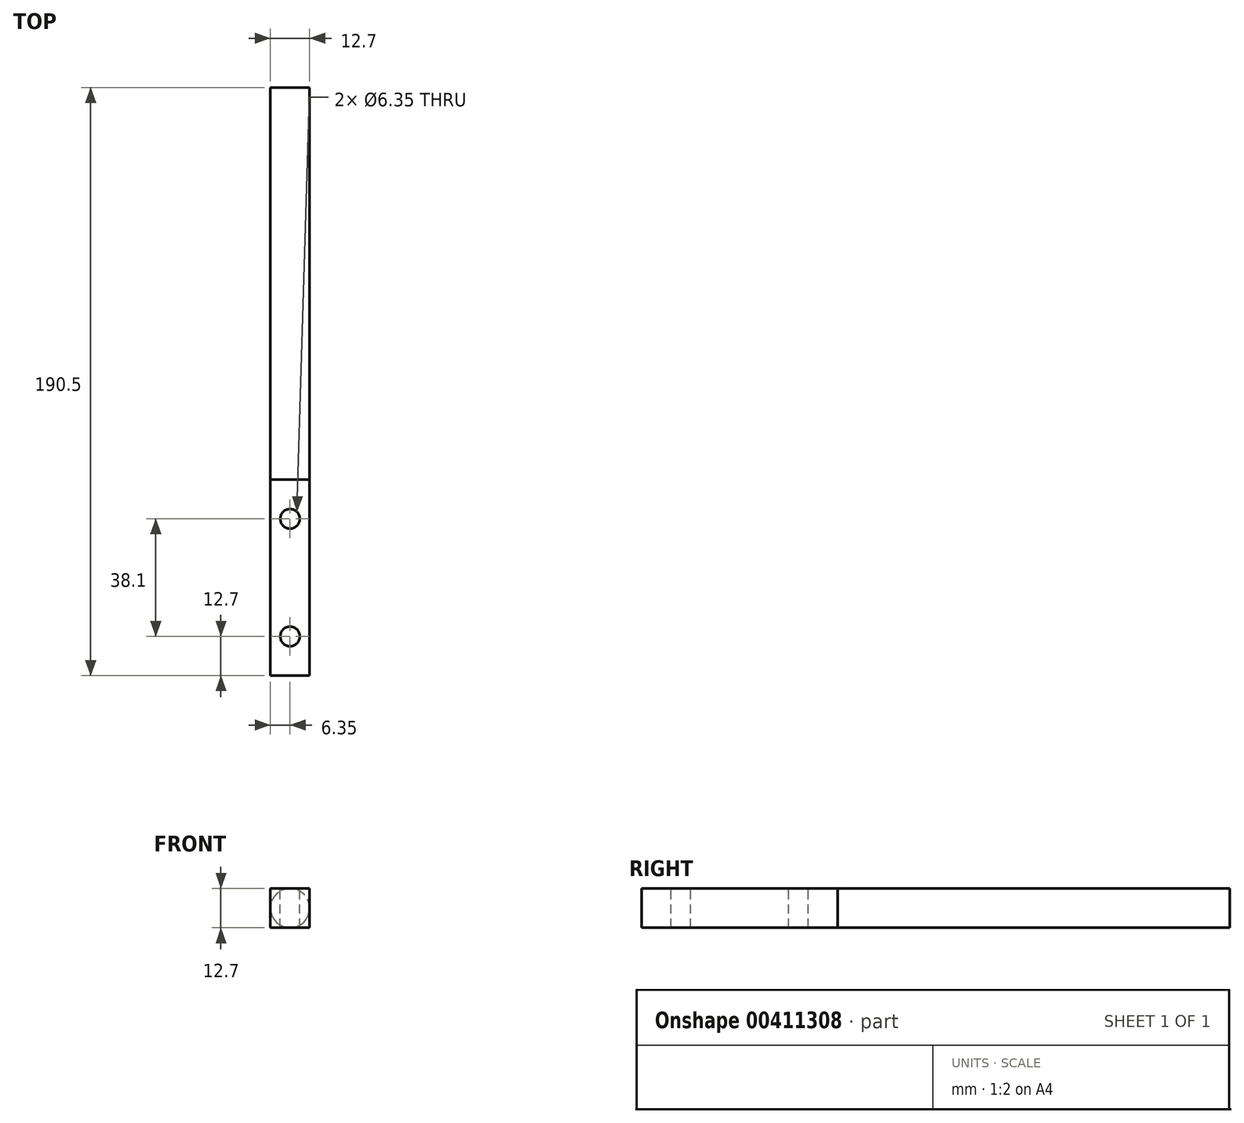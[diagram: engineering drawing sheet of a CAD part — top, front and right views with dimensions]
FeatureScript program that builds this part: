
annotation { "Feature Type Name" : "Feature", "Feature Type Description" : "" }
export const myFeature = defineFeature(function(context is Context, id is Id, definition is map)
    precondition{}
    {
        {
            var Q0;
            Q0=qCreatedBy(makeId("Right.planeOp"),FACE);
            var sketch = newSketch(context, id + "F0", { "sketchPlane" : qUnion([Q0])});
            skLineSegment(sketch, "E0.bottom", {"start": v(0, 0) * mm, "end": v(63.5, 0) * mm});
            skLineSegment(sketch, "E0.top", {"start": v(0, 12.7) * mm, "end": v(63.5, 12.7) * mm});
            skLineSegment(sketch, "E0.left", {"start": v(0, 0) * mm, "end": v(0, 12.7) * mm});
            skLineSegment(sketch, "E0.right", {"start": v(63.5, 0) * mm, "end": v(63.5, 12.7) * mm});
            skSolve(sketch);
        }
        {
            var Q0;
            Q0=makeQuery(id+"F0.imprint","IMPRINT",FACE,{"disambiguationData":[TD([[makeQuery(id+"F0.imprint","IMPRINT",EDGE,{"derivedFrom":sQuery(id+"F0.wireOp",EDGE,"E0.bottom")}),1.0]])]});
            extrude(context, id + "F1", {"entities" : qUnion([Q0]), "endBound" : BoundingType.SYMMETRIC, "depth" : 12.7 * mm});
        }
        {
            var Q0;
            Q0=makeQuery(id+"F1.opExtrude","SWEPT_FACE",FACE,{"disambiguationData":[OSD([sQuery(id+"F0.wireOp",EDGE,"E0.top")])]});
            var sketch = newSketch(context, id + "F2", { "sketchPlane" : qUnion([Q0])});
            skLineSegment(sketch, "E1", {"start": v(0, 0) * mm, "end": v(0, 12.7) * mm, "construction": true});
            skPoint(sketch, "E1.endSnap0", {"position": v(0, 0) * mm});
            skCircle(sketch, "E2", {"center": v(0, 12.7) * mm, "radius": 3.18 * mm});
            skLineSegment(sketch, "E3", {"start": v(0, 12.7) * mm, "end": v(0, 50.8) * mm, "construction": true});
            skCircle(sketch, "E4", {"center": v(0, 50.8) * mm, "radius": 3.18 * mm});
            skSolve(sketch);
        }
        {
            var Q0;
            Q0=makeQuery(id+"F2.imprint","IMPRINT",FACE,{"disambiguationData":[TD([[makeQuery(id+"F2.imprint","IMPRINT",EDGE,{"derivedFrom":sQuery(id+"F2.wireOp",EDGE,"E4")}),1.0]])]});
            var Q1;
            Q1=makeQuery(id+"F2.imprint","IMPRINT",FACE,{"disambiguationData":[TD([[makeQuery(id+"F2.imprint","IMPRINT",EDGE,{"derivedFrom":sQuery(id+"F2.wireOp",EDGE,"E2")}),1.0]])]});
            extrude(context, id + "F3", {"entities" : qUnion([Q0, Q1]), "operationType" : NewBodyOperationType.REMOVE, "oppositeDirection" : true, "depth" : 25.4 * mm});
        }
        {
            var Q0;
            Q0=makeQuery(id+"F1.opExtrude","SWEPT_FACE",FACE,{"disambiguationData":[OSD([sQuery(id+"F0.wireOp",EDGE,"E0.right")])]});
            var sketch = newSketch(context, id + "F4", { "sketchPlane" : qUnion([Q0])});
            skCircle(sketch, "E5", {"center": v(0, 6.35) * mm, "radius": 6.35 * mm});
            skPoint(sketch, "E5.centerSnap0", {"position": v(6.35, 6.35) * mm});
            skSolve(sketch);
        }
        {
            var Q0;
            Q0 = qSketchRegion(id + "F4", true);
            extrude(context, id + "F5", {"entities" : qUnion([Q0]), "operationType" : NewBodyOperationType.ADD, "depth" : 127 * mm});
        }
    });
